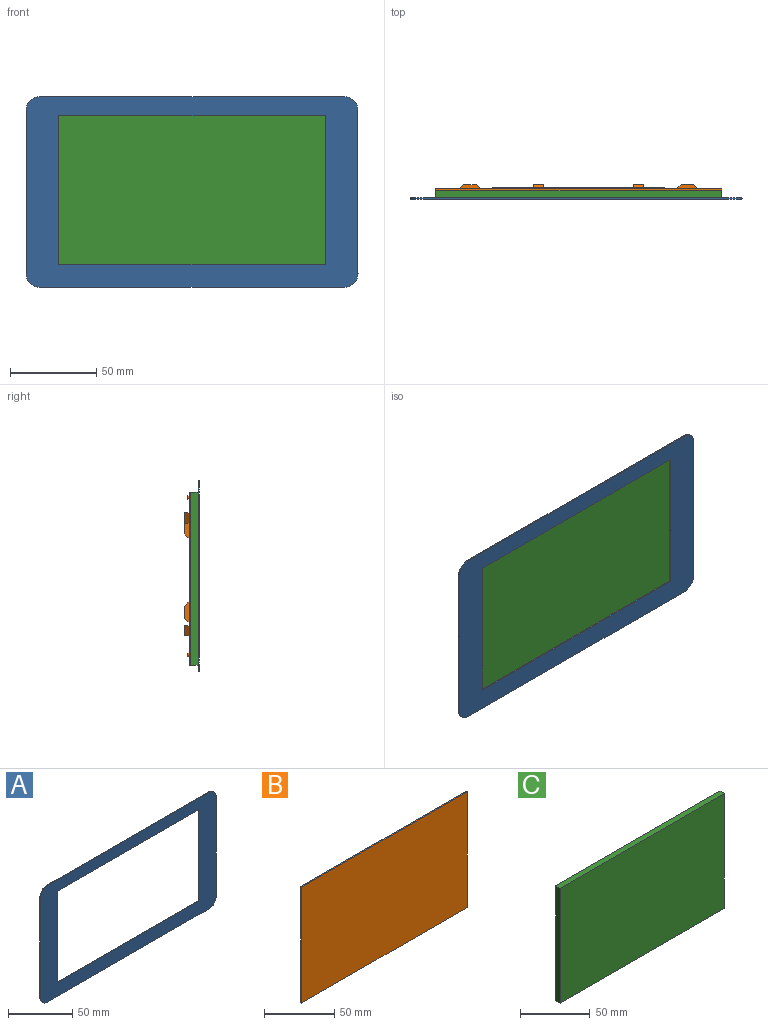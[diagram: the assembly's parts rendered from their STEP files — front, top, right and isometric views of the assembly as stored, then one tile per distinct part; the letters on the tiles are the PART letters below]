
ASSEMBLY  parts=3 mates=3
PART A: 14 faces, bbox 193x0.7x110.8 mm
  f0: plane 177.2x0.7mm, normal (0,0,1), area 124mm2, adj f1,f11,f12,f13
  f1: cylinder r=7.88mm len=7.88mm, axis (0,1,0), area 8.7mm2, adj f0,f2,f12,f13
  f2: plane 95x0.7mm, normal (-1,0,0), area 66.5mm2, adj f1,f3,f12,f13
  f3: cylinder r=7.88mm len=7.88mm, axis (0,1,0), area 8.7mm2, adj f2,f4,f12,f13
  f4: plane 177.2x0.7mm, normal (0,0,-1), area 124mm2, adj f3,f5,f12,f13
  f5: cylinder r=7.88mm len=7.88mm, axis (0,1,0), area 8.7mm2, adj f4,f6,f12,f13
  f6: plane 95x0.7mm, normal (1,0,0), area 66.5mm2, adj f5,f11,f12,f13
  f7: plane 86.72x0.7mm, normal (-1,0,0), area 60.7mm2, adj f8,f10,f12,f13
  f8: plane 154.88x0.7mm, normal (0,0,1), area 108.4mm2, adj f7,f9,f12,f13
  f9: plane 86.72x0.7mm, normal (1,0,0), area 60.7mm2, adj f8,f10,f12,f13
  f10: plane 154.88x0.7mm, normal (0,0,-1), area 108.4mm2, adj f7,f9,f12,f13
  f11: cylinder r=7.88mm len=7.88mm, axis (0,1,0), area 8.7mm2, adj f0,f6,f12,f13
  f12: plane 192.96x110.76mm, normal (0,-1,0), area 7887.8mm2, adj f0,f1,f2,f3,f4,f5,f6,f7
  f13: plane 192.96x110.76mm, normal (0,1,0), area 7887.8mm2, adj f0,f1,f2,f3,f4,f5,f6,f7
PART B: 56 faces, bbox 166.2x3.5x100.6 mm
  f0: plane 100.6x1mm, normal (1,0,0), area 100.6mm2, adj f1,f3,f4,f5
  f1: plane 166.2x1mm, normal (0,0,1), area 166.2mm2, adj f0,f2,f4,f5
  f2: plane 100.6x1mm, normal (-1,0,0), area 100.6mm2, adj f1,f3,f4,f5
  f3: plane 166.2x1mm, normal (0,0,-1), area 166.2mm2, adj f0,f2,f4,f5
  f4: plane 166.2x100.6mm, normal (0,1,0), area 15815.4mm2, adj f0,f1,f2,f3,f6,f7,f9,f10
  f5: plane 166.2x100.6mm, normal (0,-1,0), area 16719.7mm2, adj f0,f1,f2,f3
  f6: plane 12x2.5mm, normal (0,0,-1), area 23.8mm2, adj f4,f8,f44,f45
  f7: plane 12x2.5mm, normal (0,0,1), area 23.8mm2, adj f4,f8,f44,f45
  f8: plane 7x6mm, normal (0,1,0), area 42mm2, adj f6,f7,f44,f45
  f9: plane 12x2.5mm, normal (0,0,-1), area 23.8mm2, adj f4,f11,f38,f39
  f10: plane 12x2.5mm, normal (0,0,1), area 23.8mm2, adj f4,f11,f38,f39
  f11: plane 7x6mm, normal (0,1,0), area 42mm2, adj f9,f10,f38,f39
  f12: plane 12x2.5mm, normal (0,0,-1), area 23.8mm2, adj f4,f14,f30,f31
  f13: plane 12x2.5mm, normal (0,0,1), area 23.8mm2, adj f4,f14,f30,f31
  f14: plane 7x6mm, normal (0,1,0), area 42mm2, adj f12,f13,f30,f31
  f15: plane 12x2.5mm, normal (0,0,-1), area 23.8mm2, adj f4,f17,f36,f37
  f16: plane 12x2.5mm, normal (0,0,1), area 23.8mm2, adj f4,f17,f36,f37
  f17: plane 7x6mm, normal (0,1,0), area 42mm2, adj f15,f16,f36,f37
  f18: plane 12x2.5mm, normal (-1,0,0), area 23.8mm2, adj f4,f20,f42,f43
  f19: plane 12x2.5mm, normal (1,0,0), area 23.8mm2, adj f4,f20,f42,f43
  f20: plane 7x6mm, normal (0,1,0), area 42mm2, adj f18,f19,f42,f43
  f21: plane 12x2.5mm, normal (-1,0,0), area 23.8mm2, adj f4,f23,f40,f41
  f22: plane 12x2.5mm, normal (1,0,0), area 23.8mm2, adj f4,f23,f40,f41
  f23: plane 7x6mm, normal (0,1,0), area 42mm2, adj f21,f22,f40,f41
  f24: plane 12x2.5mm, normal (-1,0,0), area 23.7mm2, adj f4,f26,f32,f33
  f25: plane 12x2.5mm, normal (1,0,0), area 23.7mm2, adj f4,f26,f32,f33
  f26: plane 7x6mm, normal (0,1,0), area 42mm2, adj f24,f25,f32,f33
  f27: plane 12x2.5mm, normal (-1,0,0), area 23.7mm2, adj f4,f29,f34,f35
  f28: plane 12x2.5mm, normal (1,0,0), area 23.7mm2, adj f4,f29,f34,f35
  f29: plane 7x6mm, normal (0,1,0), area 42mm2, adj f27,f28,f34,f35
  f30: plane 6x2.5mm, normal (0.71,0.71,0), area 21.2mm2, adj f4,f12,f13,f14
  f31: plane 6x2.5mm, normal (-0.71,0.71,0), area 21.2mm2, adj f4,f12,f13,f14
  f32: plane 6x2.5mm, normal (0,0.71,-0.71), area 21.2mm2, adj f4,f24,f25,f26
  f33: plane 6x2.5mm, normal (0,0.71,0.71), area 21.2mm2, adj f4,f24,f25,f26
  f34: plane 6x2.5mm, normal (0,0.71,0.71), area 21.2mm2, adj f4,f27,f28,f29
  f35: plane 6x2.5mm, normal (0,0.71,-0.71), area 21.2mm2, adj f4,f27,f28,f29
  f36: plane 6x2.5mm, normal (-0.71,0.71,0), area 21.2mm2, adj f4,f15,f16,f17
  f37: plane 6x2.5mm, normal (0.71,0.71,0), area 21.2mm2, adj f4,f15,f16,f17
  f38: plane 6x2.5mm, normal (-0.71,0.71,0), area 21.2mm2, adj f4,f9,f10,f11
  f39: plane 6x2.5mm, normal (0.71,0.71,0), area 21.2mm2, adj f4,f9,f10,f11
  f40: plane 6x2.5mm, normal (0,0.71,-0.71), area 21.2mm2, adj f4,f21,f22,f23
  f41: plane 6x2.5mm, normal (0,0.71,0.71), area 21.2mm2, adj f4,f21,f22,f23
  f42: plane 6x2.5mm, normal (0,0.71,-0.71), area 21.2mm2, adj f4,f18,f19,f20
  f43: plane 6x2.5mm, normal (0,0.71,0.71), area 21.2mm2, adj f4,f18,f19,f20
  f44: plane 6x2.5mm, normal (-0.71,0.71,0), area 21.2mm2, adj f4,f6,f7,f8
  f45: plane 6x2.5mm, normal (0.71,0.71,0), area 21.2mm2, adj f4,f6,f7,f8
  f46: plane 98x1mm, normal (0,0,1), area 98mm2, adj f4,f47,f49,f50
  f47: cylinder r=1mm len=2mm, axis (0,-1,0), area 3.1mm2, adj f4,f46,f48,f50
  f48: plane 98x1mm, normal (0,0,-1), area 98mm2, adj f4,f47,f49,f50
  f49: cylinder r=1mm len=2mm, axis (0,-1,0), area 3.1mm2, adj f4,f46,f48,f50
  f50: plane 100x2mm, normal (0,1,0), area 199.1mm2, adj f46,f47,f48,f49
  f51: plane 63x1mm, normal (0,0,1), area 63mm2, adj f4,f52,f54,f55
  f52: cylinder r=1mm len=2mm, axis (0,-1,0), area 3.1mm2, adj f4,f51,f53,f55
  f53: plane 63x1mm, normal (0,0,-1), area 63mm2, adj f4,f52,f54,f55
  f54: cylinder r=1mm len=2mm, axis (0,-1,0), area 3.1mm2, adj f4,f51,f53,f55
  f55: plane 65x2mm, normal (0,1,0), area 129.1mm2, adj f51,f52,f53,f54
PART C: 6 faces, bbox 166.2x4.3x100.6 mm
  f0: plane 100.6x4.26mm, normal (1,0,0), area 428.6mm2, adj f1,f3,f4,f5
  f1: plane 166.2x4.26mm, normal (0,0,1), area 708mm2, adj f0,f2,f4,f5
  f2: plane 100.6x4.26mm, normal (-1,0,0), area 428.6mm2, adj f1,f3,f4,f5
  f3: plane 166.2x4.26mm, normal (0,0,-1), area 708mm2, adj f0,f2,f4,f5
  f4: plane 166.2x100.6mm, normal (0,1,0), area 16719.7mm2, adj f0,f1,f2,f3
  f5: plane 166.2x100.6mm, normal (0,-1,0), area 16719.7mm2, adj f0,f1,f2,f3
PLACE A t=(11.25,22.18,-27.34)mm
PLACE B t=(506.41,26.44,-27.35)mm
PLACE C t=(259.88,22.18,-29.85)mm
MATE planar C.f5 <-> A.f13  axis (0,-1,0) through (12.74,22.18,-28.89)mm
MATE slider A.f13 <-> C.f5  axis (0,1,0) through (99.85,22.18,28.04)mm
MATE fastened C.f4 <-> B.f5  axis (0,1,0) through (12.74,26.44,-28.89)mm
